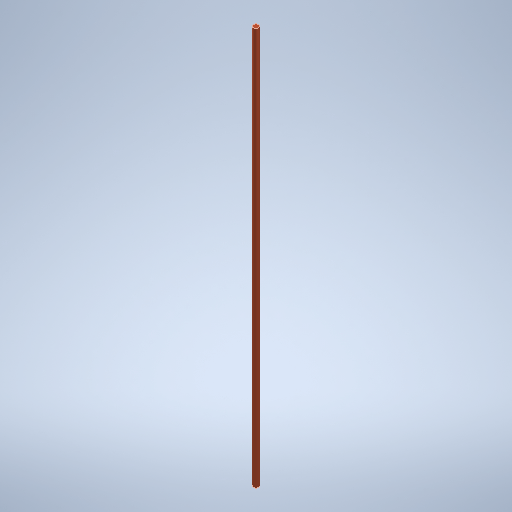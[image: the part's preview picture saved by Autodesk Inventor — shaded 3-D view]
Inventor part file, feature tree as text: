
AUTODESK INVENTOR PART (.ipt)
format: ipt  version: 2025.1 (Build 291241020, 241B)  size: 248,832 bytes
history: native  units: in
note: dims shown in document units (in); Inventor stores cm internally (conversion verified against a paired STEP export)
features: extrude x1, sketch x1
ambient origin geometry x8: Origin, YZ Plane, XZ Plane, XY Plane, X Axis, Y Axis, Z Axis, Center Point
bodies: Solid1 (feature_tree)
feature tree (2):
  extrude  "Extrusion1"  Depth=36.875in TaperAngle=0.0deg
  sketch  "Sketch1"  dims[d0=0.5in d1=36.875in d2=0.0in]
